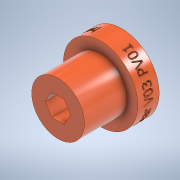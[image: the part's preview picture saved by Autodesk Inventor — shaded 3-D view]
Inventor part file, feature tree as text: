
AUTODESK INVENTOR PART (.ipt)
format: ipt  version: 2022.2 (Build 262287010, 287A)  size: 1,632,768 bytes
history: native  units: in
note: dims shown in document units (in); Inventor stores cm internally (conversion verified against a paired STEP export)
features: sketch x9, extrude x6, hole x2, plane x1, emboss x1
ambient origin geometry x8: Origin, YZ Plane, XZ Plane, XY Plane, X Axis, Y Axis, Z Axis, Center Point
bodies: Solid1 (feature_tree)
feature tree (19):
  extrude  "Extrusion1"  Depth=0.5in TaperAngle=0.0deg
  extrude  "Extrusion2"  Depth=0.75in TaperAngle=0.0deg
  extrude  "Base"  Depth=0.5in TaperAngle=0.0deg
  hole  "Hole1"  [1 undecoded]
  hole  "Hole2"  [1 undecoded]
  plane  "Work Plane1"
  emboss  "Emboss2"
  extrude  "Extrusion4"  Depth=0.25in TaperAngle=0.0deg
  extrude  "Extrusion5"  [1 undecoded]
  extrude  "Extrusion6"  [1 undecoded]
  sketch  "Sketch1"  dims[d0=0.5in d1=1.0in d2=0.0in]
  sketch  "Sketch2"  dims[d3=1.24in d4=0.75in d5=0.0in]
  sketch  "Sketch3"  dims[d6=1.75in d7=0.5in d8=0.0in]
  sketch  "Sketch6"  dims[d13=0.244in]
  sketch  "Sketch7"  dims[d14=0.17in d15=0.75in d16=0.5in d17=0.093in d18=0.5635in d19=1.0in d20=0.8108in]
  sketch  "Sketch8"  dims[d21=0.249in d22=0.75in d23=0.26in d24=0.2411in d25=0.5635in d26=0.31in d27=0.0in d28=0.1in d29=0.0in]
  sketch  "Sketch9"  dims[d30=1.0in d31=0.0in d32=0.51in]
  sketch  "Sketch10"  dims[d33=0.0in d34=0.0in d35=0.25in d36=0.0in]
  sketch  "Sketch11"
note: 4 required parameter values undecoded (feature->parameter linkage not recoverable at this tier; creation-order binding heuristic only, values carry confidence <= 0.55)
